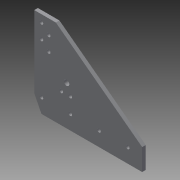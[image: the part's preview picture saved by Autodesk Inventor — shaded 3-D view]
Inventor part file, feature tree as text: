
AUTODESK INVENTOR PART (.ipt)
format: ipt  version: 2015 SP1 (Build 190203100, 203)  size: 142,336 bytes
history: native  units: in
note: dims shown in document units (in); Inventor stores cm internally (conversion verified against a paired STEP export)
features: extrude x3, sketch x3
ambient origin geometry x8: Origin, YZ Plane, XZ Plane, XY Plane, X Axis, Y Axis, Z Axis, Center Point
bodies: Body1 (feature_tree)
feature tree (6):
  extrude  "Extrusion4"  Depth=6.0in
  extrude  "Extrusion5"  Depth=2.0in
  extrude  "Extrusion6"  Depth=0.25in
  sketch  "Sketch1"  dims[d0=7.5in d1=6.0in]
  sketch  "Sketch3"  dims[d2=0.5in d3=2.0in]
  sketch  "Sketch4"  dims[d8=1.0in d9=1.0in d10=1.5in d11=90.0deg d12=1.5in d13=90.0deg d14=6.0in d15=180.0deg d16=1.5in d17=0.5in d18=0.5in d19=0.5in d20=0.5in d21=0.5in d22=1.0in d23=1.5in d24=2.0in d25=0.25in d26=0.25in d29=0.25in d30=0.25in d31=0.25in d32=0.25in d35=2.0in d36=2.0in d38=0.25in d39=0.25in d46=1.0in d47=1.0in d48=0.25in d49=0.0in d50=1.0in d51=0.5in d52=0.25in d53=0.0in d54=0.375in d55=1.0in d56=2.0625in d57=2.0625in d58=2.75in d59=0.75in d60=0.25in d61=0.25in d62=0.375in d63=0.25in d64=0.0in]
